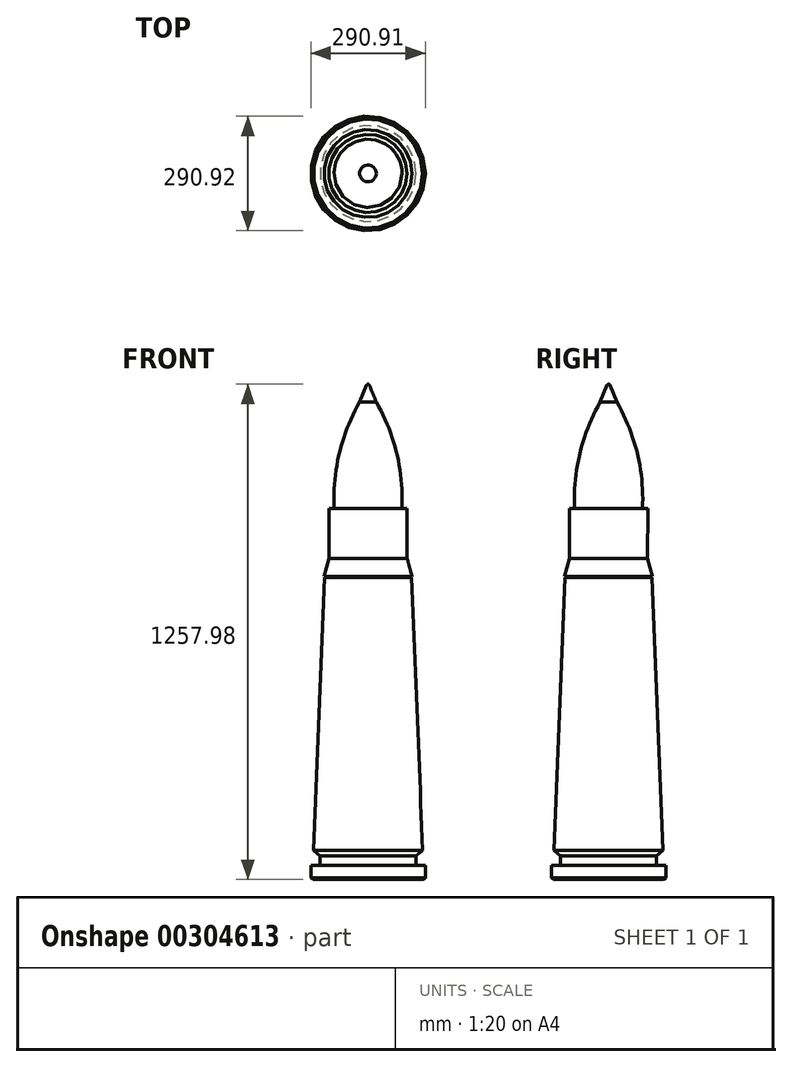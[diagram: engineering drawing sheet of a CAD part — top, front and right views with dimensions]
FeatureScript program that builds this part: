
annotation { "Feature Type Name" : "Feature", "Feature Type Description" : "" }
export const myFeature = defineFeature(function(context is Context, id is Id, definition is map)
    precondition{}
    {
        {
            var Q0;
            Q0=qCreatedBy(makeId("Front.planeOp"),FACE);
            var sketch = newSketch(context, id + "F0", { "sketchPlane" : qUnion([Q0])});
            skLineSegment(sketch, "E0", {"start": v(32.8, -468.9) * mm, "end": v(10.07, -468.9) * mm});
            skLineSegment(sketch, "E1", {"start": v(10.07, -468.9) * mm, "end": v(10.07, -443.5) * mm});
            skLineSegment(sketch, "E2", {"start": v(-1.58, 263.87) * mm, "end": v(26.39, -429.99) * mm});
            skLineSegment(sketch, "E3.MirrorCS", {"start": v(-0.68, 266.18) * mm, "end": v(-13, 311.92) * mm});
            skArc(sketch, "E4", {"start": v(-109.02, 752.03) * mm, "mid": v(-110.42, 753.75) * mm, "end": v(-112.55, 754.4) * mm});
            skLineSegment(sketch, "E5", {"start": v(-91.2, 708.63) * mm, "end": v(-109.02, 752.03) * mm});
            skLineSegment(sketch, "E6.MirrorCS", {"start": v(26.39, -429.99) * mm, "end": v(10.07, -443.5) * mm});
            skLineSegment(sketch, "E7.MirrorCS", {"start": v(-13, 311.92) * mm, "end": v(-13, 438.92) * mm});
            skLineSegment(sketch, "E8.MirrorCS", {"start": v(-13, 438.92) * mm, "end": v(-26.34, 438.92) * mm});
            skArc(sketch, "E9.trimOffspring", {"start": v(-26.23, 438.92) * mm, "mid": v(-39.44, 578.42) * mm, "end": v(-91.2, 708.63) * mm});
            skLineSegment(sketch, "E10", {"start": v(33.28, -500.45) * mm, "end": v(33.28, -468.7) * mm});
            skLineSegment(sketch, "E11", {"start": v(27.72, -503.5) * mm, "end": v(33.28, -500.45) * mm});
            skLineSegment(sketch, "E12", {"start": v(-112.17, -484.87) * mm, "end": v(-3.71, -484.87) * mm});
            skLineSegment(sketch, "E13", {"start": v(27.72, -503.5) * mm, "end": v(-3.71, -503.5) * mm});
            skLineSegment(sketch, "E14", {"start": v(-3.71, -503.5) * mm, "end": v(-3.71, -484.87) * mm});
            skLineSegment(sketch, "E15", {"start": v(-112.17, -484.87) * mm, "end": v(-112.55, 754.4) * mm});
            skPoint(sketch, "E16", {"position": v(-112.45, 438.92) * mm});
            skSolve(sketch);
        }
        {
            var Q0;
            Q0=sQuery(id+"F0.wireOp",EDGE,"55e46fe0-a3e0-4288-8775-2feb8b04cdf8");
            var Q1;
            Q1=sQuery(id+"F0.wireOp",EDGE,"E11");
            var Q2;
            Q2=sQuery(id+"F0.wireOp",EDGE,"E10");
            var Q3;
            Q3=sQuery(id+"F0.wireOp",EDGE,"E0");
            var Q4;
            Q4=sQuery(id+"F0.wireOp",EDGE,"E1");
            var Q5;
            Q5=sQuery(id+"F0.wireOp",EDGE,"E6.MirrorCS");
            var Q6;
            Q6=sQuery(id+"F0.wireOp",EDGE,"E2");
            var Q7;
            Q7=sQuery(id+"F0.wireOp",EDGE,"E3.MirrorCS");
            var Q8;
            Q8=sQuery(id+"F0.wireOp",EDGE,"E7.MirrorCS");
            var Q9;
            Q9=sQuery(id+"F0.wireOp",EDGE,"E8.MirrorCS");
            var Q10;
            Q10=sQuery(id+"F0.wireOp",EDGE,"E5");
            var Q11;
            Q11=sQuery(id+"F0.wireOp",EDGE,"E4");
            var Q12;
            Q12=sQuery(id+"F0.wireOp",EDGE,"E15");
            revolve(context, id + "F1", {"bodyType" : ToolBodyType.SURFACE, "operationType" : NewBodyOperationType.ADD, "surfaceEntities" : qUnion([Q0, Q1, Q2, Q3, Q4, Q5, Q6, Q7, Q8, Q9, Q10, Q11]), "axis" : qUnion([Q12]), "revolveType" : RevolveType.FULL});
        }
        {
            var Q0;
            Q0=sQuery(id+"F0.wireOp",EDGE,"E9.trimOffspring");
            var Q1;
            Q1=sQuery(id+"F0.wireOp",EDGE,"E15");
            revolve(context, id + "F2", {"bodyType" : ToolBodyType.SURFACE, "surfaceEntities" : qUnion([Q0]), "axis" : qUnion([Q1]), "revolveType" : RevolveType.FULL});
        }
    });
